# Revit family: Fixture_Support_Elongated_Barrel_Fitting_EZCarry_Horizontal-Zurn-ZE1201-ND4
name_source: partatom
category: Plumbing Fixtures
units: mm (PartAtom-declared; Revit-internal decimal feet)

## family parameters
Always vertical = Yes
Cut with Voids When Loaded = Yes
Maintain Annotation Orientation = No
OmniClass Number = 23.45.55.11
OmniClass Title = Sanitary Components
Part Type = Normal
Room Calculation Point = No
Round Connector Dimension = Use Radius
Shared = No
Work Plane-Based = No

## types (1)
- ZE1201-ND4
    Approx. Weight (Lbs) = 122.00 lb
    Assembly Code = D2030400
    CW Connection = No
    CWFU = 0
    Calc Angle = 360.00°
    Calc Angle_2 = 360.00°
    Calc Length = 34.875 "
    Calc Length_2 = 3.125 "
    Coupling Material = ABS - Zurn - Plastic
    Coupling Radius (Outer) = 2.313 "
    Default Elevation = 20 "
    Description = ELONGATED BARREL FITTING 38 [965] EZCARRY® ADJUSTABLE HORIZONTAL HIGH PERFORMANCE SIPHON JET NO-HUB WATER CLOSET CARRIER SYSTEM
    Dimension_B = 38 "
    Dimension_K = 4.125 "
    Dimension_N = 8.813 "
    Fitting Flange Distance = 11 "
    HW Connection = No
    HWFU = 0
    Half Side Length_A = 34.875 "
    Half Side Length_B = 3.125 "
    Main Material = Iron - Zurn -Cast - Painted - Blue
    Manufacturer = Zurn Water, LLC
    Manufacurer Brand = Zurn
    Model = ZE1201-ND4
    Modified Date = 03/27/2026
    N_Dimension = 14.188 "
    Pipe Size_A Inside Radius = 2.013 "
    Pipe Size_A Nominal Radius = 2 "
    Pipe Size_A Outer Radius = 2.25 "
    Product Documentation Link = https://files.zurn.com
    Product Installation Sheet URL = https://files.zurn.com
    Product Page URL = https://www.zurn.com
    Product data url = https://www.bimobject.com
    Rotational Connector Distance = 4.75 "
    URL = www.zurn.com
    Vent Connection = Yes
    Vent Connector Radius = 1 "
    Vent Diameter (Actual) = 2.375 "
    Vent Diameter (Nominal) = 2 "
    WFU = 0
    Waste Connection = Yes
    Water Closet Inlet Radius = 1.5 "
    Width = 17.125 "
    ZE1201-NR4 = Yes

## geometry (parser evidence)
native form markers: Blend x8, Sweep x99
no freeform markers — native parametric forms only
